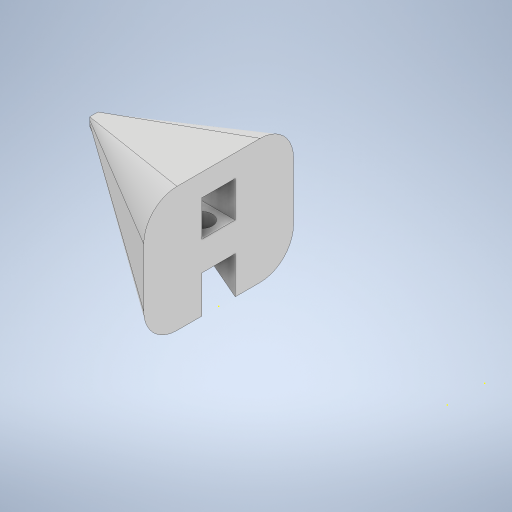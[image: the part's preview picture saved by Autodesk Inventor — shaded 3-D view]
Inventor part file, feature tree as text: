
AUTODESK INVENTOR PART (.ipt)
format: ipt  version: 2024 (Build 280153000, 153)  size: 589,824 bytes
history: native  units: mm
features: sketch x29, extrude x23, chamfer x3, plane x3, split x3, move_body x3, boolean_combine x1, fillet x1, loft x1, other x1
ambient origin geometry x8: Origin, YZ Plane, XZ Plane, XY Plane, X Axis, Y Axis, Z Axis, Center Point
bodies: Solid1 (feature_tree), Solid2 (feature_tree), Solid3 (feature_tree), Solid4 (feature_tree), Solid5 (feature_tree), Solid6 (feature_tree), Solid7 (feature_tree)
feature tree (68):
  extrude  "Extrusion1"  Depth=16.0mm
  sketch  "Sketch2"  dims[d2=15.0mm d3=0.0mm d4=10.0mm]
  extrude  "Extrusion2"  Depth=10.0mm
  chamfer  "Chamfer1"  Distance=21.25mm
  extrude  "Extrusion3"  Depth=10.0mm TaperAngle=0.0deg
  extrude  "Extrusion4"  Depth=7.0mm TaperAngle=0.0deg
  extrude  "Extrusion5"  Depth=1.0mm TaperAngle=0.0deg
  chamfer  "Chamfer2"  Distance=6.0mm Angle=45.0deg
  sketch  "Sketch6"  dims[d14=7.0mm d15=11.5mm d16=0.0mm]
  extrude  "Extrusion6"  Depth=15.0mm
  extrude  "Extrusion7"  Depth=45.25mm TaperAngle=0.0deg
  chamfer  "Chamfer3"  Distance=11.5mm Angle=45.0deg
  sketch  "Sketch9"  dims[d26=3.3mm d27=45.25mm d28=0.0mm d29=11.5mm d30=5.5mm d31=45.0deg]
  extrude  "Extrusion8"  Depth=65.75mm TaperAngle=0.0deg
  extrude  "Extrusion9"  Depth=9.0mm TaperAngle=0.0deg
  extrude  "Extrusion10"  Depth=13.0mm TaperAngle=0.0deg
  sketch  "Sketch13"  dims[d43=24.0mm d44=21.0mm d45=0.0mm]
  extrude  "Extrusion11"  Depth=21.0mm TaperAngle=0.0deg
  extrude  "Extrusion12"  TaperAngle=0.0deg  [1 undecoded]
  extrude  "Extrusion13"  Depth=6.0mm TaperAngle=0.0deg
  plane  "Work Plane1"
  split  "Split1"
  move_body  "Move Body1"
  extrude  "Extrusion14"  Depth=10.0mm TaperAngle=0.0deg
  move_body  "Move Body2"
  extrude  "Extrusion15"  TaperAngle=0.0deg  [1 undecoded]
  plane  "Work Plane2"
  split  "Split2"
  move_body  "Move Body3"
  boolean_combine  "Combine1"
  extrude  "Extrusion16"  Depth=0.5mm TaperAngle=0.0deg
  extrude  "Extrusion17"  Depth=10.0mm TaperAngle=0.0deg
  extrude  "Extrusion19"  Depth=1.0mm TaperAngle=0.0deg
  extrude  "Extrusion20"  Depth=15.0mm
  sketch  "Sketch24"  dims[d91=0.0mm d92=90.0deg d93=0.0mm d94=90.0deg d97=4.0mm]
  sketch  "Sketch25"  dims[d98=4.326mm d99=3.5mm]
  extrude  "Extrusion23"  Depth=4.0mm
  extrude  "Extrusion24"  TaperAngle=0.0deg  [1 undecoded]
  plane  "Work Plane3"
  sketch  "Sketch26"  dims[d100=4.0mm d101=0.0mm d102=2.5mm]
  fillet  "Fillet5"  Radius=4.0mm
  loft  "Loft1"
  split  "Split3"
  sketch  "Sketch28"
  extrude  "Extrusion25"  Depth=4.0mm
  extrude  "Extrusion26"  TaperAngle=0.0deg  [1 undecoded]
  sketch  "Sketch1"  dims[d0=36.0mm d1=16.0mm]
  sketch  "Sketch3"  dims[d5=10.0mm]
  sketch  "Sketch4"  dims[d6=3.3mm d7=21.25mm d8=0.0mm]
  sketch  "Sketch5"  dims[d9=10.0mm d10=5.5mm d11=45.0deg d12=10.0mm d13=0.0mm]
  sketch  "Sketch7"  dims[d17=3.3mm d18=1.0mm d19=0.0mm d20=6.0mm d21=11.5mm d22=45.0deg]
  sketch  "Sketch8"  dims[d23=15.0mm d24=0.0mm d25=9.0mm]
  sketch  "Sketch10"  dims[d32=2.0mm d33=65.75mm d34=0.0mm]
  sketch  "Sketch11"  dims[d35=0.5mm d36=0.0mm d37=9.0mm d38=0.0mm]
  sketch  "Sketch12"  dims[d39=0.5mm d40=0.0mm d41=13.0mm d42=0.0mm]
  sketch  "Sketch14"  dims[d46=12.25mm d47=-12.0mm d48=0.0mm d49=0.0mm]
  sketch  "Sketch15"  dims[d50=30.0mm d51=0.0mm d52=6.0mm d53=0.0mm d54=0.0mm]
  sketch  "Sketch16"  dims[d56=10.0mm d57=20.0mm d58=0.0mm]
  sketch  "Sketch17"  dims[d59=3.75mm d60=-10.0mm d61=0.0mm d62=0.0mm]
  sketch  "Sketch18"  dims[d64=0.5mm d65=0.0mm d66=0.5mm d67=0.0mm]
  sketch  "Sketch19"  dims[d71=3.0mm d72=10.0mm d73=0.0mm]
  sketch  "Sketch20"  dims[d74=10.0mm d75=0.0mm d81=1.0mm d82=0.0mm]
  sketch  "Sketch22"  dims[d83=1.0mm d84=0.0mm d86=15.0mm]
  sketch  "Sketch23"  dims[d89=1.0mm d90=4.0mm]
  other  "Edges1"
  sketch  "Sketch27"  dims[d103=4.0mm d104=0.0mm d63=0.0mm]
  sketch  "Sketch29"
  sketch  "Sketch30"
note: 4 required parameter values undecoded (feature->parameter linkage not recoverable at this tier; creation-order binding heuristic only, values carry confidence <= 0.55)
